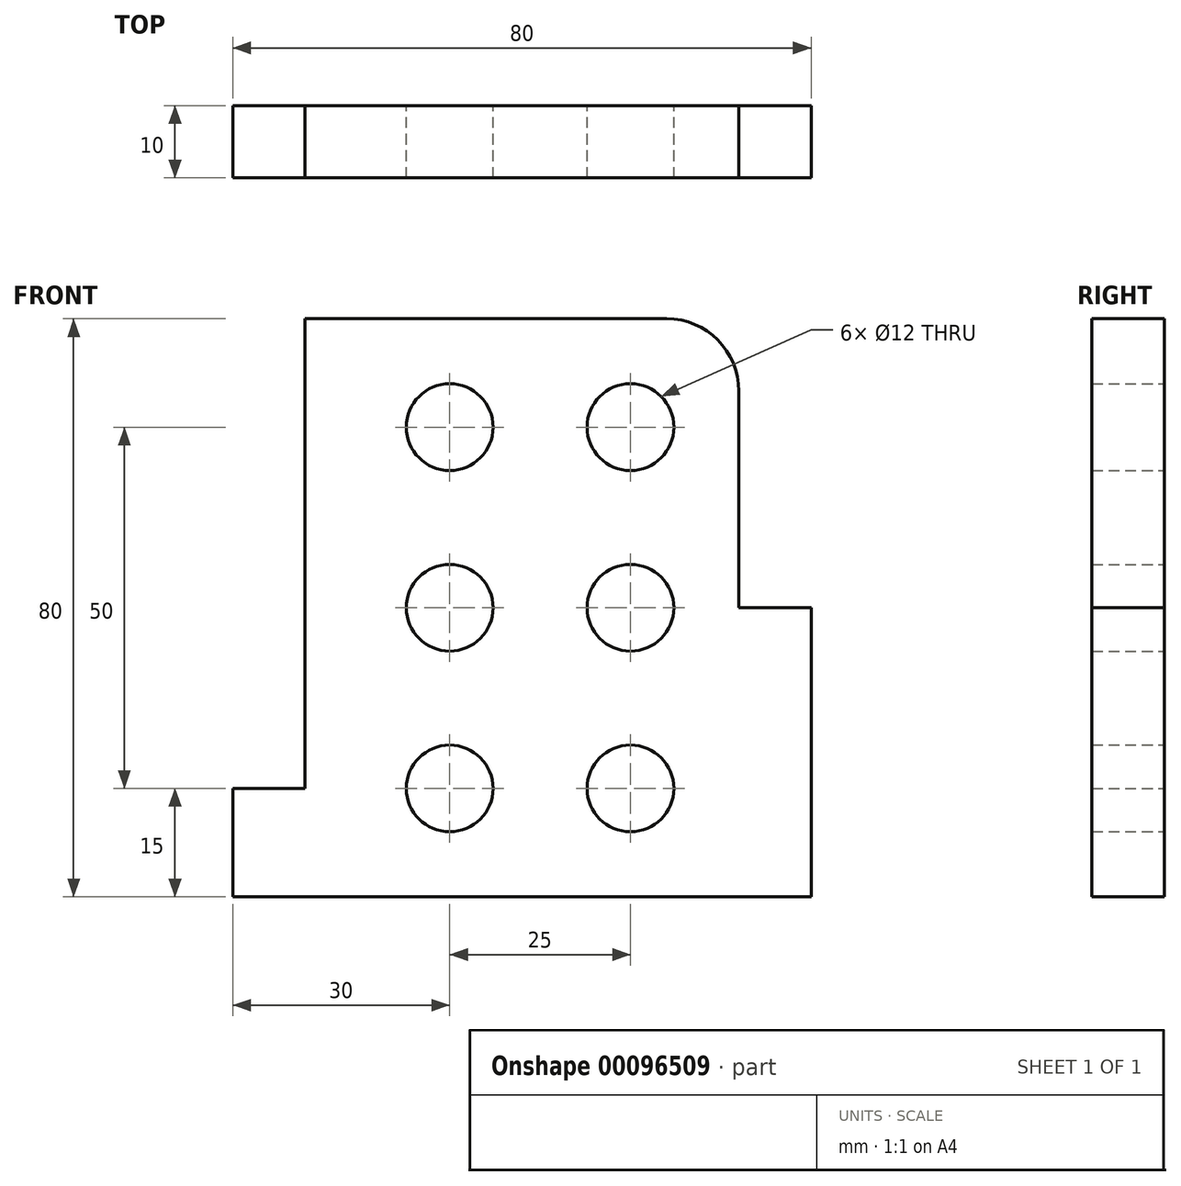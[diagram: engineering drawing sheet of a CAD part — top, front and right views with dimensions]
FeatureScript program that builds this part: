
annotation { "Feature Type Name" : "Feature", "Feature Type Description" : "" }
export const myFeature = defineFeature(function(context is Context, id is Id, definition is map)
    precondition{}
    {
        {
            var Q0;
            Q0=qCreatedBy(makeId("Front.planeOp"),FACE);
            var sketch = newSketch(context, id + "F0", { "sketchPlane" : qUnion([Q0])});
            skLineSegment(sketch, "E0", {"start": v(0, 0) * mm, "end": v(0, 15) * mm});
            skLineSegment(sketch, "E1", {"start": v(0, 15) * mm, "end": v(10, 15) * mm});
            skLineSegment(sketch, "E2", {"start": v(10, 15) * mm, "end": v(10, 80) * mm});
            skLineSegment(sketch, "E3", {"start": v(10, 80) * mm, "end": v(60, 80) * mm});
            skLineSegment(sketch, "E4", {"start": v(70, 70) * mm, "end": v(70, 40) * mm});
            skLineSegment(sketch, "E5", {"start": v(70, 40) * mm, "end": v(80, 40) * mm});
            skLineSegment(sketch, "E6", {"start": v(80, 40) * mm, "end": v(80, 0) * mm});
            skLineSegment(sketch, "E7", {"start": v(80, 0) * mm, "end": v(0, 0) * mm});
            skCircle(sketch, "E8", {"center": v(30, 15) * mm, "radius": 6 * mm});
            skCircle(sketch, "E9", {"center": v(55, 15) * mm, "radius": 6 * mm});
            skCircle(sketch, "E10", {"center": v(55, 40) * mm, "radius": 6 * mm});
            skCircle(sketch, "E11", {"center": v(30, 40) * mm, "radius": 6 * mm});
            skCircle(sketch, "E12", {"center": v(30, 65) * mm, "radius": 6 * mm});
            skCircle(sketch, "E13", {"center": v(55, 65) * mm, "radius": 6 * mm});
            skPoint(sketch, "E14.visualSharp", {"position": v(70, 80) * mm});
            skArc(sketch, "E14.filletArc", {"start": v(70, 70) * mm, "mid": v(67.07, 77.07) * mm, "end": v(60, 80) * mm});
            skSolve(sketch);
        }
        {
            var Q0;
            Q0 = qSketchRegion(id + "F0", true);
            extrude(context, id + "F1", {"entities" : qUnion([Q0]), "depth" : 10 * mm});
        }
    });
